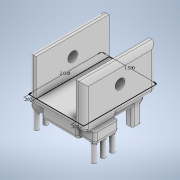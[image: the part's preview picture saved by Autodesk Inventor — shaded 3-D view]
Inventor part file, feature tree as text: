
AUTODESK INVENTOR PART (.ipt)
format: ipt  version: 2020 (Build 240168000, 168)  size: 705,536 bytes
history: native  units: in
note: dims shown in document units (in); Inventor stores cm internally (conversion verified against a paired STEP export)
features: sketch x5, extrude x4, fillet x4, hole x2
ambient origin geometry x8: Origin, YZ Plane, XZ Plane, XY Plane, X Axis, Y Axis, Z Axis, Center Point
bodies: Solid1 (feature_tree)
feature tree (15):
  sketch  "Sketch1"  dims[d0=1.5in d1=2.0in]
  extrude  "Extrusion1"  Depth=2.0in
  extrude  "Extrusion2"  Depth=0.2in
  hole  "Hole1"  [1 undecoded]
  extrude  "Extrusion3"  Depth=0.0625in
  extrude  "Extrusion4"  Depth=0.0625in
  hole  "Hole2"  [1 undecoded]
  fillet  "Fillet1"  Radius=0.25in
  fillet  "Fillet2"  Radius=0.25in
  fillet  "Fillet3"  [1 undecoded]
  fillet  "Fillet4"  Radius=0.7874in
  sketch  "Sketch2"  dims[d2=0.2in d3=0.2in]
  sketch  "Sketch3"  dims[d4=1.0in d5=0.0in d6=0.2in d7=0.0in]
  sketch  "Sketch4"  dims[d8=0.5in]
  sketch  "Sketch5"  dims[d9=0.266in d10=0.75in d11=0.438in d12=0.25in d13=0.5635in d14=1.0in d15=0.8108in d16=1.0in d17=1.8425in d18=0.25in d19=0.25in d20=0.25in d21=180.0deg d22=0.7874in d23=0.0in d24=0.7874in d25=0.7874in d26=0.7874in d27=0.7874in d29=1.7717in d30=0.65in d31=0.3335in d32=0.0in d33=0.25in d34=0.25in d35=0.25in d36=0.7874in d37=0.7874in d38=0.1181in d39=0.1181in d40=0.1181in d41=0.1181in d42=0.1181in d43=0.1181in d44=0.4331in d45=0.0in d46=0.6693in d47=0.25in d48=0.089in d49=0.146in d50=0.75in d51=0.188in d52=0.5635in d53=0.224in d54=0.0in d55=0.125in d56=0.125in d57=0.0625in d58=0.0625in]
note: 3 required parameter values undecoded (feature->parameter linkage not recoverable at this tier; creation-order binding heuristic only, values carry confidence <= 0.55)
